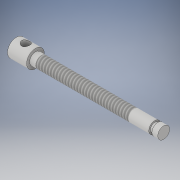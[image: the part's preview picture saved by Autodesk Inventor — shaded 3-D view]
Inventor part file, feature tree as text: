
AUTODESK INVENTOR PART (.ipt)
format: ipt  version: 2017 (Build 210142000, 142)  size: 136,704 bytes
history: native  units: in
note: dims shown in document units (in); Inventor stores cm internally (conversion verified against a paired STEP export)
features: sketch x3, hole x2, revolve x1, thread x1
ambient origin geometry x8: Origin, YZ Plane, XZ Plane, XY Plane, X Axis, Y Axis, Z Axis, Center Point
bodies: Solid1 (feature_tree)
feature tree (7):
  revolve  "Revolution1"  [1 undecoded]
  thread  "Thread1"  [1 undecoded]
  hole  "Hole1"  [1 undecoded]
  hole  "Hole2"  [1 undecoded]
  sketch  "Sketch1"  dims[d0=0.375in d1=0.8125in d2=6.25in]
  sketch  "Sketch2"  dims[d4=0.25in d7=0.1875in]
  sketch  "Sketch3"  dims[d8=0.1295in d9=90.0deg d10=0.25in d11=3.9375in d12=0.25in d13=3.9375in d14=0.8705in d15=0.3438in d16=0.3438in d17=0.75in d18=0.375in d19=0.25in d20=0.5635in d21=1.0in d22=0.8108in d23=0.4062in d24=0.3438in d26=0.375in d27=0.4062in d28=0.375in d29=0.3438in d30=0.75in d31=0.375in d32=0.25in d33=0.5635in d34=1.0in d35=0.8108in]
note: 4 required parameter values undecoded (feature->parameter linkage not recoverable at this tier; creation-order binding heuristic only, values carry confidence <= 0.55)